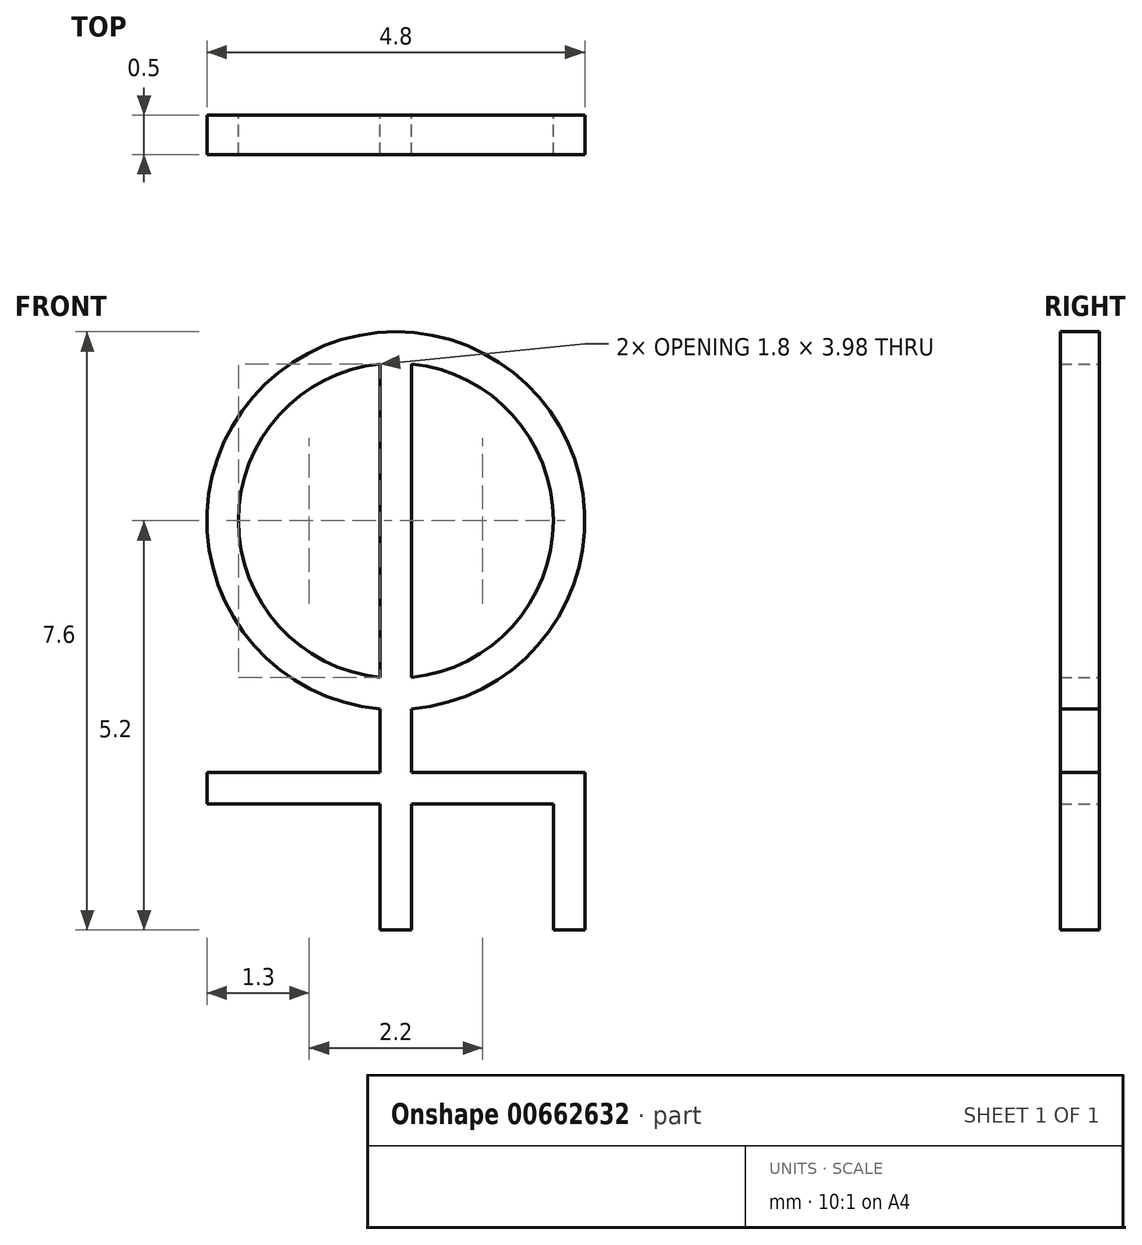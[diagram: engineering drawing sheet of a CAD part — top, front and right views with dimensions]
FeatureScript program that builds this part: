
annotation { "Feature Type Name" : "Feature", "Feature Type Description" : "" }
export const myFeature = defineFeature(function(context is Context, id is Id, definition is map)
    precondition{}
    {
        {
            var Q0;
            Q0=qCreatedBy(makeId("Front.planeOp"),FACE);
            var sketch = newSketch(context, id + "F0", { "sketchPlane" : qUnion([Q0])});
            skArc(sketch, "E0", {"start": v(0.2, -1.99) * mm, "mid": v(2, 0) * mm, "end": v(0.2, 1.99) * mm});
            skArc(sketch, "E1.0", {"start": v(0.2, -2.4) * mm, "mid": v(0, 2.4) * mm, "end": v(-0.2, -2.4) * mm});
            skLineSegment(sketch, "E2", {"start": v(-0.2, 1.99) * mm, "end": v(-0.2, -1.99) * mm});
            skLineSegment(sketch, "E3", {"start": v(0.2, 1.99) * mm, "end": v(0.2, -1.99) * mm});
            skLineSegment(sketch, "E4", {"start": v(0.2, -5.2) * mm, "end": v(-0.2, -5.2) * mm});
            skLineSegment(sketch, "E5", {"start": v(-2.4, -3.2) * mm, "end": v(-0.2, -3.2) * mm});
            skLineSegment(sketch, "E6", {"start": v(2.4, -3.2) * mm, "end": v(2.4, -5.2) * mm});
            skLineSegment(sketch, "E7", {"start": v(2.4, -5.2) * mm, "end": v(2, -5.2) * mm});
            skLineSegment(sketch, "E8", {"start": v(2, -5.2) * mm, "end": v(2, -3.6) * mm});
            skLineSegment(sketch, "E9", {"start": v(2, -3.6) * mm, "end": v(0.2, -3.6) * mm});
            skLineSegment(sketch, "E10", {"start": v(-2.4, -3.2) * mm, "end": v(-2.4, -3.6) * mm});
            skArc(sketch, "E11.trimOffspring", {"start": v(-0.2, 1.99) * mm, "mid": v(-2, 0) * mm, "end": v(-0.2, -1.99) * mm});
            skLineSegment(sketch, "E12.trimOffspring", {"start": v(-0.2, -2.4) * mm, "end": v(-0.2, -3.2) * mm});
            skLineSegment(sketch, "E13.trimOffspring", {"start": v(0.2, -2.4) * mm, "end": v(0.2, -3.2) * mm});
            skLineSegment(sketch, "E14.trimOffspring", {"start": v(-0.2, -3.6) * mm, "end": v(-0.2, -5.2) * mm});
            skLineSegment(sketch, "E15.trimOffspring", {"start": v(0.2, -3.2) * mm, "end": v(2.4, -3.2) * mm});
            skLineSegment(sketch, "E16.trimOffspring", {"start": v(0.2, -3.6) * mm, "end": v(0.2, -5.2) * mm});
            skLineSegment(sketch, "E17.trimOffspring", {"start": v(-0.2, -3.6) * mm, "end": v(-2.4, -3.6) * mm});
            skSolve(sketch);
        }
        {
            var Q0;
            Q0=makeQuery(id+"F0.imprint","IMPRINT",FACE,{"disambiguationData":[TD([[makeQuery(id+"F0.imprint","IMPRINT",EDGE,{"derivedFrom":sQuery(id+"F0.wireOp",EDGE,"E0")}),-1.0]])]});
            extrude(context, id + "F1", {"entities" : qUnion([Q0]), "depth" : .5 * mm, "offsetDistance" : 25 * mm});
        }
    });
